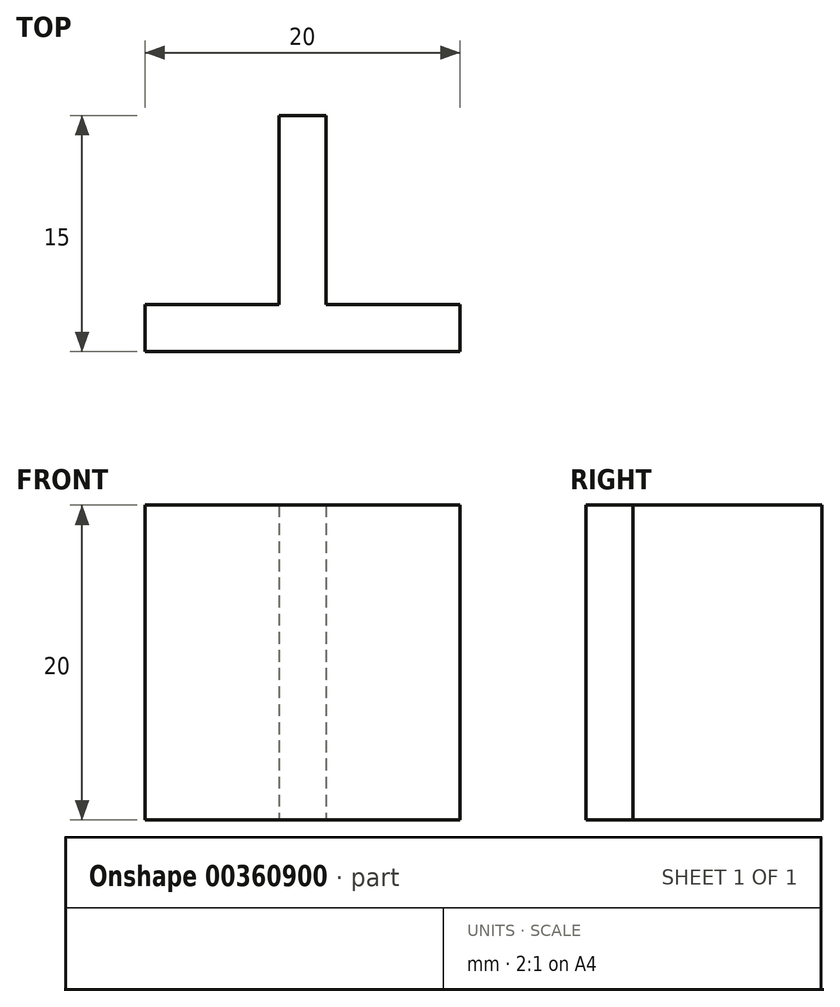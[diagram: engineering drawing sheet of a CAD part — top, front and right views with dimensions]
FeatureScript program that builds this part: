
annotation { "Feature Type Name" : "Feature", "Feature Type Description" : "" }
export const myFeature = defineFeature(function(context is Context, id is Id, definition is map)
    precondition{}
    {
        {
            var Q0;
            Q0=qCreatedBy(makeId("Top.planeOp"),FACE);
            var sketch = newSketch(context, id + "F0", { "sketchPlane" : qUnion([Q0])});
            skLineSegment(sketch, "E0", {"start": v(0, 0) * mm, "end": v(20, 0) * mm});
            skLineSegment(sketch, "E1", {"start": v(20, 0) * mm, "end": v(20, 3) * mm});
            skLineSegment(sketch, "E2", {"start": v(20, 3) * mm, "end": v(11.5, 3) * mm});
            skLineSegment(sketch, "E3", {"start": v(11.5, 3) * mm, "end": v(11.5, 15) * mm});
            skLineSegment(sketch, "E4", {"start": v(11.5, 15) * mm, "end": v(8.5, 15) * mm});
            skLineSegment(sketch, "E5", {"start": v(8.5, 15) * mm, "end": v(8.5, 3) * mm});
            skLineSegment(sketch, "E6", {"start": v(8.5, 3) * mm, "end": v(0, 3) * mm});
            skLineSegment(sketch, "E7", {"start": v(0, 3) * mm, "end": v(0, 0) * mm});
            skSolve(sketch);
        }
        {
            var Q0;
            Q0 = qSketchRegion(id + "F0", true);
            extrude(context, id + "F1", {"entities" : qUnion([Q0]), "depth" : 20 * mm});
        }
    });
